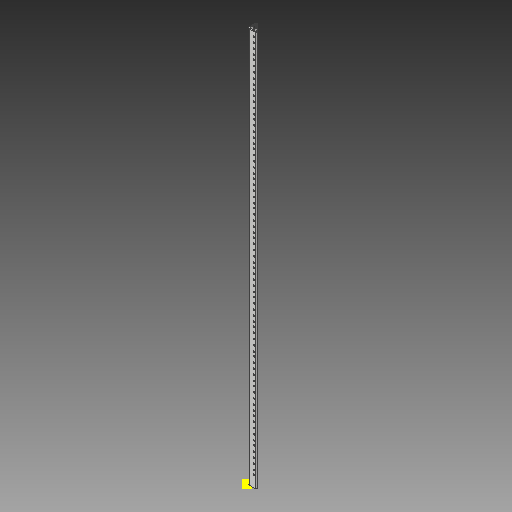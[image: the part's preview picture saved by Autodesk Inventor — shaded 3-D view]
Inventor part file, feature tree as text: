
AUTODESK INVENTOR PART (.ipt)
format: ipt  version: 2017 (Build 210142000, 142)  size: 520,192 bytes
history: native  units: in
note: dims shown in document units (in); Inventor stores cm internally (conversion verified against a paired STEP export)
features: other x3, sketch x2
ambient origin geometry x8: Origin, YZ Plane, XZ Plane, XY Plane, X Axis, Y Axis, Z Axis, Center Point
bodies: Solid1 (feature_tree)
feature tree (5):
  other  "squareHoleRail20U.ipt"
  other  "Solid1::squareHoleRail20U.ipt"
  other  "TaggingFeature1"
  sketch  "Sketch3"  dims[d0=0.3937in]
  sketch  "Sketch4"
